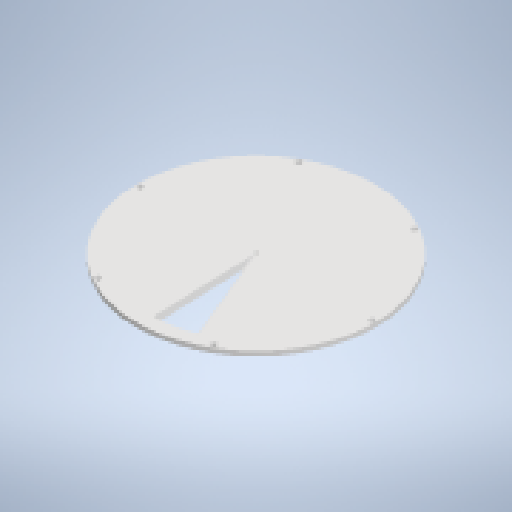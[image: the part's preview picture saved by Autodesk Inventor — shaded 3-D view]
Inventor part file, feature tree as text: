
AUTODESK INVENTOR PART (.ipt)
format: ipt  version: 2025 (Build 290162010, 162A)  size: 168,448 bytes
history: native  units: mm
features: sketch x5, reference x4, other x4, extrude x2, hole x2, chamfer x2
ambient origin geometry x8: Origin, YZ Plane, XZ Plane, XY Plane, X Axis, Y Axis, Z Axis, Center Point
bodies: Volumenkörper1 (feature_tree)
feature tree (19):
  extrude  "Extrusion1"  Depth=3.0mm
  hole  "Bohrung1"  [1 undecoded]
  extrude  "Extrusion2"  Depth=3.0mm TaperAngle=45.0deg
  chamfer  "Fasen1"  [1 undecoded]
  sketch  "Skizze4"  dims[d22=1.3mm d23=2.4mm d24=4.0mm d25=2.0mm d26=90.0deg d27=10.0mm d28=20.594885mm]
  chamfer  "Fasen2"  [1 undecoded]
  hole  "Bohrung2"  [1 undecoded]
  sketch  "Skizze1"  dims[d0=3.0mm d1=0.0mm d2=78.5mm]
  reference  "Referenz1"
  sketch  "Skizze2"  dims[d7=2.4mm d8=6.0mm d9=4.4mm d10=2.0mm d11=90.0deg d12=8.0mm d13=20.594885mm d14=0.0mm d15=0.0mm]
  sketch  "Skizze - Runde Anordnung1"  dims[d3=60.0mm d5=360.0deg]
  sketch  "Skizze3"  dims[d16=2.0mm d17=3.0mm d18=45.0deg d19=1.0mm d20=2.0mm d21=45.0deg]
  reference  "Referenz2"
  reference  "Referenz4"
  reference  "Referenz5"
  other  "<userpath>\GIT\pillbox\Baugruppe1.iam"
  other  "Baugruppe1.iam"
  other  "Bauteil2:1"
  other  "Bauteil1:1"
note: 4 required parameter values undecoded (feature->parameter linkage not recoverable at this tier; creation-order binding heuristic only, values carry confidence <= 0.55)
